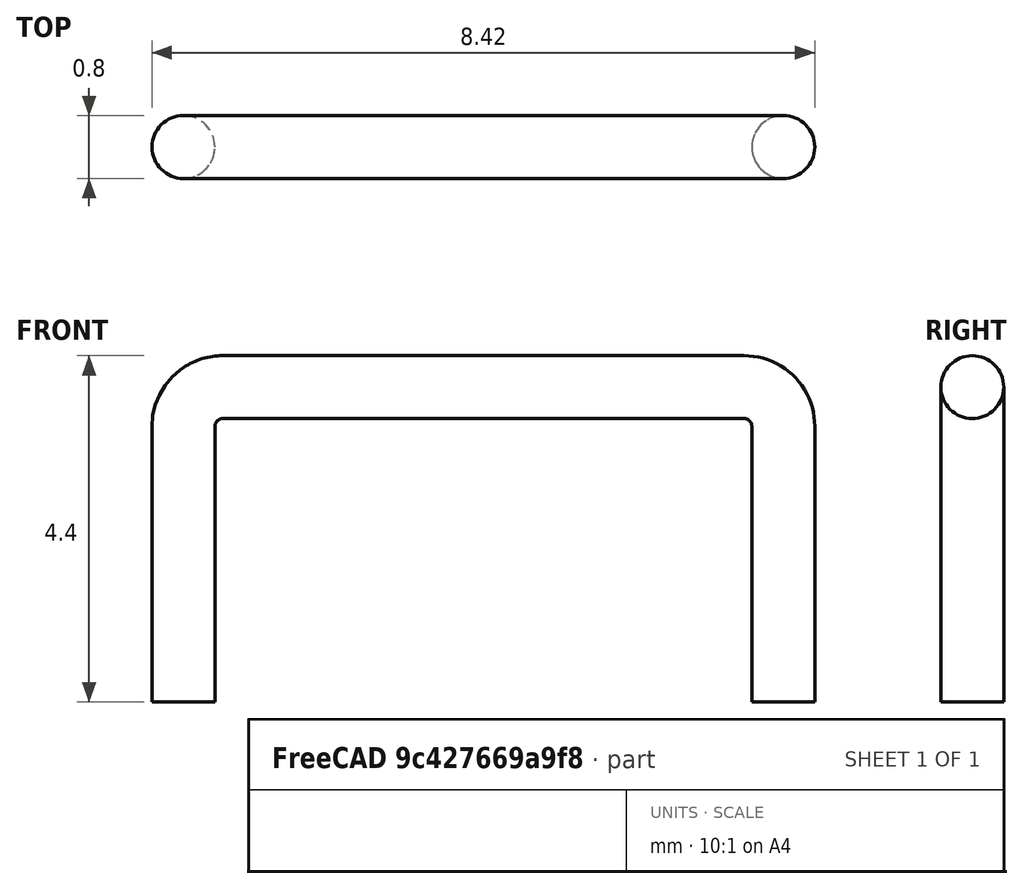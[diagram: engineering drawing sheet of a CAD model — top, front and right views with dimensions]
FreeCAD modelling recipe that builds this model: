
FCSTD DOCUMENT  (FreeCAD 0.18.4R)
Label: WireBridge_P7.62mm
License: All rights reserved
LicenseURL: http://en.wikipedia.org/wiki/All_rights_reserved
objects: Sketcher::SketchObject×2, PartDesign::AdditivePipe×1, PartDesign::Body×1
note: 5 computed .brp shape members not serialized (recipe doc carries the construction recipe); baked Part::Feature solids carry a one-line shape summary decoded from their .brp

FEATURE [Sketcher::SketchObject] Sketch  label="CrossSection"
  MapMode = 5
  Support = -> [XY_Plane]
  sketch-geometry (1):
    g0: Circle CenterX=0 CenterY=0 CenterZ=0 NormalX=0 NormalY=0 NormalZ=1 AngleXU=0 Radius=0.4
  constraints (2):
    c: Diameter(g0) = 0.8
    c: Coincident(g0,g-1)
FEATURE [Sketcher::SketchObject] Sketch001  label="Path"
  MapMode = 5
  Placement = pos=(0,0,0) rot=(1,0,0;1.5708rad)
  Support = -> [XZ_Plane]
  sketch-geometry (5):
    g0: LineSegment StartX=0 StartY=0 StartZ=0 EndX=0 EndY=3.5 EndZ=0
    g1: LineSegment StartX=0.5 StartY=4 StartZ=0 EndX=7.12 EndY=4 EndZ=0
    g2: LineSegment StartX=7.62 StartY=3.5 StartZ=0 EndX=7.62 EndY=0 EndZ=0
    g3: ArcOfCircle CenterX=7.12 CenterY=3.5 CenterZ=0 NormalX=0 NormalY=0 NormalZ=1 AngleXU=0 Radius=0.5 StartAngle=-9e-16 EndAngle=1.5708
    g4: ArcOfCircle CenterX=0.5 CenterY=3.5 CenterZ=0 NormalX=0 NormalY=0 NormalZ=1 AngleXU=0 Radius=0.5 StartAngle=1.5708 EndAngle=3.14159
  constraints (13):
    c: Coincident(g-1,g0)
    c: Horizontal(g1)
    c: PointOnObject(g2,g-1)
    c: Vertical(g2)
    c: Tangent(g1,g3) = 1.5708
    c: Tangent(g2,g3) = 1.5708
    c: Tangent(g0,g4) = 1.5708
    c: Tangent(g1,g4) = 1.5708
    c: DistanceX(g0,g2) = 7.62
    c: Vertical(g0)
    c: DistanceY(g0,g1) = 4
    c: Radius(g3) = 0.5
    c: Radius(g4) = 0.5
FEATURE [PartDesign::AdditivePipe] AdditivePipe
  AuxilleryCurvelinear = true
  AuxillerySpineTangent = false
  Binormal = (0,0,0)
  Mode = 0
  Profile = -> Sketch
  Refine = true
  Spine = -> Sketch001
  SpineTangent = false
  Transformation = 0
  Transition = 0
FEATURE [PartDesign::Body] Body
  Group = -> [Sketch,Sketch001,AdditivePipe]
  Origin = -> Origin
  Tip = -> AdditivePipe
